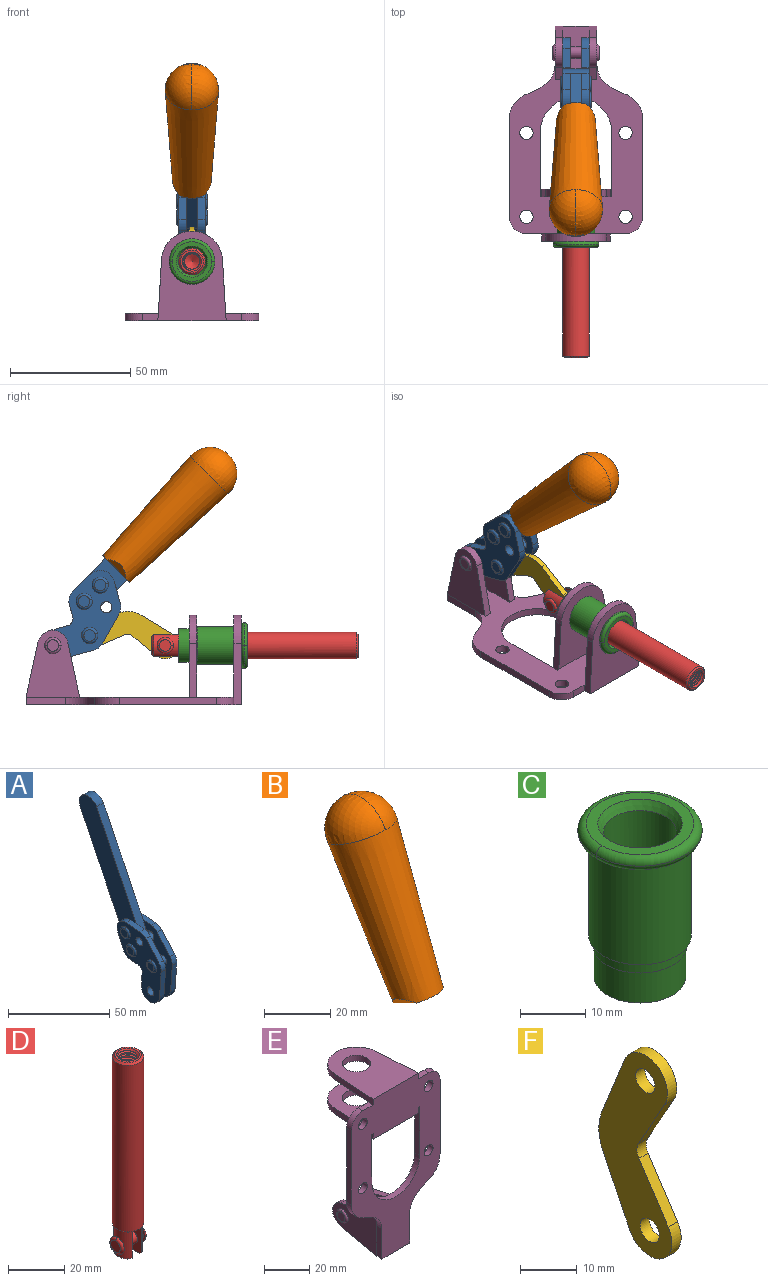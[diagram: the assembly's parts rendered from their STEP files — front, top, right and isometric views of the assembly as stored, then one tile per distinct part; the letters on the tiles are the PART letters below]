
ASSEMBLY  parts=6 mates=6
PART A: 59 faces, bbox 12.9x60.2x99.6 mm
  f0: torus R=2.39mm, axis (-1,0,0), area 14.9mm2, adj f20,f43,f51
  f1: torus R=2.39mm, axis (-1,0,0), area 14.9mm2, adj f19,f42,f51
  f2: torus R=2.39mm, axis (-1,0,0), area 14.9mm2, adj f18,f35,f51
  f3: torus R=2.39mm, axis (-1,0,0), area 14.9mm2, adj f14,f17,f23
  f4: torus R=2.39mm, axis (-1,0,0), area 14.9mm2, adj f13,f16,f23
  f5: torus R=2.39mm, axis (-1,0,0), area 14.9mm2, adj f12,f15,f23
  f6: cylinder r=2.39mm len=4.78mm, axis (1,0,0), area 46.5mm2, adj f48,f50,f51
  f7: cylinder r=2.39mm len=4.78mm, axis (1,0,0), area 46.5mm2, adj f50,f51
  f8: cylinder r=6.35mm len=12.68mm, axis (1,0,0), area 61.8mm2, adj f38,f39,f50,f51
  f9: cylinder r=2.39mm len=4.78mm, axis (-1,0,0), area 70.5mm2, adj f46,f50
  f10: cylinder r=2.39mm len=4.78mm, axis (-1,0,0), area 46.5mm2, adj f23,f45,f46
  f11: cylinder r=2.39mm len=4.78mm, axis (-1,0,0), area 46.5mm2, adj f23,f46
  f12: plane 4.78x4.78mm, normal (1,0,0), area 17.9mm2, adj f5,f15
  f13: plane 4.78x4.78mm, normal (1,0,0), area 17.9mm2, adj f4,f16
  f14: plane 4.78x4.78mm, normal (1,0,0), area 17.9mm2, adj f3,f17
  f15: torus R=2.39mm, axis (-1,0,0), area 14.9mm2, adj f5,f12,f23
  f16: torus R=2.39mm, axis (-1,0,0), area 14.9mm2, adj f4,f13,f23
  f17: torus R=2.39mm, axis (-1,0,0), area 14.9mm2, adj f3,f14,f23
  f18: plane 4.78x4.78mm, normal (-1,0,0), area 17.9mm2, adj f2,f35
  f19: plane 4.78x4.78mm, normal (-1,0,0), area 17.9mm2, adj f1,f42
  f20: plane 4.78x4.78mm, normal (-1,0,0), area 17.9mm2, adj f0,f43
  f21: plane 2.26x0.2mm, normal (1,0,0), area 0.2mm2, adj f31,f44
  f22: plane 2.26x0.2mm, normal (-1,0,0), area 0.2mm2, adj f41,f44
  f23: plane 39.37x30.77mm, normal (1,0,0), area 565.5mm2, adj f3,f4,f5,f10,f11,f15,f16,f17
  f24: cylinder r=6.1mm len=4.15mm, axis (-1,0,0), area 14.7mm2, adj f23,f25,f32,f46
  f25: plane 10.25x9.01mm, normal (0,-0.75,0.66), area 42.3mm2, adj f23,f24,f26,f46
  f26: cylinder r=6.35mm len=4.64mm, axis (-1,0,0), area 15.6mm2, adj f23,f25,f27,f46
  f27: plane 15.84x3.1mm, normal (0,-1,-0.07), area 49.2mm2, adj f23,f26,f28,f46
  f28: cylinder r=6.35mm len=12.68mm, axis (-1,0,0), area 61.8mm2, adj f23,f27,f29,f46
  f29: plane 8.11x3.1mm, normal (0,1,0.07), area 25.2mm2, adj f23,f28,f30,f46
  f30: cylinder r=3.05mm len=3.25mm, axis (-1,0,0), area 14.8mm2, adj f23,f29,f31,f46
  f31: plane 5.99x3.1mm, normal (0,0.07,-1), area 18.6mm2, adj f21,f23,f30,f44,f46
  f32: plane 9.5x3.1mm, normal (0,-0.07,1), area 29.5mm2, adj f23,f24,f33,f46,f47
  f33: cylinder r=6.1mm len=8.63mm, axis (-1,0,0), area 39.1mm2, adj f23,f32,f34,f47
  f34: plane 8.65x3.96mm, normal (0,0.91,-0.42), area 29.5mm2, adj f23,f33,f44,f47
  f35: torus R=2.39mm, axis (-1,0,0), area 14.9mm2, adj f2,f18,f51
  f36: plane 10.25x9.01mm, normal (0,-0.75,0.66), area 42.3mm2, adj f37,f49,f50,f51
  f37: cylinder r=6.35mm len=4.64mm, axis (1,0,0), area 15.6mm2, adj f36,f38,f50,f51
  f38: plane 15.84x3.1mm, normal (0,-1,-0.07), area 49.2mm2, adj f8,f37,f50,f51
  f39: plane 8.11x3.1mm, normal (0,1,0.07), area 25.2mm2, adj f8,f40,f50,f51
  f40: cylinder r=3.05mm len=3.25mm, axis (1,0,0), area 14.8mm2, adj f39,f41,f50,f51
  f41: plane 5.99x3.1mm, normal (0,0.07,-1), area 18.6mm2, adj f22,f40,f44,f50,f51
  f42: torus R=2.39mm, axis (-1,0,0), area 14.9mm2, adj f1,f19,f51
  f43: torus R=2.39mm, axis (-1,0,0), area 14.9mm2, adj f0,f20,f51
  f44: cylinder r=6.35mm len=12.12mm, axis (-1,0,0), area 128.9mm2, adj f21,f22,f23,f31,f34,f41,f46,f47
  f45: plane 2.65x1.35mm, normal (1,0,0), area 1mm2, adj f10,f55
  f46: plane 39.08x20.42mm, normal (-1,0,0), area 412.5mm2, adj f9,f10,f11,f24,f25,f26,f27,f28
  f47: plane 77.62x39.82mm, normal (1,0,0), area 850mm2, adj f32,f33,f34,f44,f53,f54,f55
  f48: plane 2.65x1.35mm, normal (-1,0,0), area 1mm2, adj f6,f55
  f49: cylinder r=6.1mm len=4.15mm, axis (1,0,0), area 14.7mm2, adj f36,f50,f51,f56
  f50: plane 39.08x20.42mm, normal (1,0,0), area 412.5mm2, adj f6,f7,f8,f9,f36,f37,f38,f39
  f51: plane 39.37x30.77mm, normal (-1,0,0), area 565.5mm2, adj f0,f1,f2,f6,f7,f8,f35,f36
  f52: plane 8.65x3.96mm, normal (0,0.91,-0.42), area 29.5mm2, adj f44,f51,f57,f58
  f53: plane 68.49x33.4mm, normal (0,0.9,-0.44), area 358.1mm2, adj f44,f47,f54,f58
  f54: cylinder r=6.35mm len=12.06mm, axis (1,0,0), area 93.7mm2, adj f47,f53,f55,f58
  f55: plane 68.49x33.4mm, normal (0,-0.9,0.44), area 358.1mm2, adj f44,f45,f46,f47,f48,f50,f54,f58
  f56: plane 9.5x3.1mm, normal (0,-0.07,1), area 29.5mm2, adj f49,f50,f51,f57,f58
  f57: cylinder r=6.1mm len=8.63mm, axis (1,0,0), area 39.1mm2, adj f51,f52,f56,f58
  f58: plane 77.62x39.82mm, normal (-1,0,0), area 850mm2, adj f44,f52,f53,f54,f55,f56,f57
PART B: 11 faces, bbox 22.3x42.6x64.5 mm
  f0: sphere r=11.13mm, area 411.4mm2, adj f1,f8
  f1: cone r=11.11mm half-angle=3.3deg, axis (0,0.44,0.9), area 3251.8mm2, adj f0,f7,f8,f9,f10
  f2: cylinder r=6.16mm len=11.7mm, axis (1,0,0), area 89.5mm2, adj f3,f4,f5,f6
  f3: plane 60.23x36.75mm, normal (-1,0,0), area 763.6mm2, adj f2,f4,f6,f10
  f4: plane 51.37x25.05mm, normal (0,0.9,-0.44), area 264.2mm2, adj f2,f3,f5,f10
  f5: plane 60.23x36.75mm, normal (1,0,0), area 763.6mm2, adj f2,f4,f6,f10
  f6: plane 51.37x25.05mm, normal (0,-0.9,0.44), area 264.2mm2, adj f2,f3,f5,f10
  f7: plane 9.95x5.95mm, normal (0.71,-0.31,-0.64), area 25.8mm2, adj f1,f10
  f8: sphere r=11.13mm, area 411.4mm2, adj f0,f1
  f9: plane 9.95x5.95mm, normal (-0.71,-0.31,-0.64), area 25.8mm2, adj f1,f10
  f10: plane 14.27x11.38mm, normal (0,-0.44,-0.9), area 106.7mm2, adj f1,f3,f4,f5,f6,f7,f9
PART C: 15 faces, bbox 20.6x20.6x28.7 mm
  f0: torus R=8.26mm, axis (0,0,1), area 56.8mm2, adj f1,f10,f12
  f1: torus R=8.26mm, axis (0,0,1), area 56.8mm2, adj f0,f6,f13
  f2: cylinder r=5.59mm len=25.91mm, axis (0,0,1), area 909.6mm2, adj f3,f4
  f3: cone r=6.86mm half-angle=45deg, axis (0,0,-1), area 70.2mm2, adj f2,f14
  f4: cone r=6.47mm half-angle=30deg, axis (0,0,1), area 66.7mm2, adj f2,f13
  f5: cylinder r=7.04mm len=14.07mm, axis (0,0,1), area 252.6mm2, adj f11,f14
  f6: torus R=8.26mm, axis (0,0,1), area 56.8mm2, adj f1,f12,f13
  f7: cylinder r=7.16mm len=14.33mm, axis (0,0,1), area 91.5mm2, adj f9,f11
  f8: cylinder r=7.86mm len=18.42mm, axis (0,0,1), area 909.6mm2, adj f9,f10
  f9: plane 15.72x15.72mm, normal (0,0,-1), area 33mm2, adj f7,f8
  f10: plane 16.51x16.51mm, normal (0,0,-1), area 19.9mm2, adj f0,f8,f12
  f11: plane 14.33x14.33mm, normal (0,0,-1), area 5.7mm2, adj f5,f7
  f12: torus R=8.26mm, axis (0,0,1), area 56.8mm2, adj f0,f6,f10
  f13: plane 16.51x16.51mm, normal (0,0,1), area 82.7mm2, adj f1,f4,f6
  f14: plane 14.07x14.07mm, normal (0,0,-1), area 7.8mm2, adj f3,f5
PART D: 48 faces, bbox 12.6x11.1x86.1 mm
  f0: torus R=2.41mm, axis (-1,0,0), area 15mm2, adj f30,f32,f34
  f1: torus R=2.41mm, axis (-1,0,0), area 15mm2, adj f29,f31,f33
  f2: cylinder r=5.54mm len=72.39mm, axis (0,0,1), area 2518.5mm2, adj f3,f4,f42,f43
  f3: cone r=5.54mm half-angle=45deg, axis (0,0,1), area 7.6mm2, adj f2,f5,f41
  f4: cone r=5.54mm half-angle=45deg, axis (0,0,-1), area 34.9mm2, adj f2,f39
  f5: cylinder r=5.08mm len=11.48mm, axis (0,0,1), area 108.3mm2, adj f3,f7,f8,f41
  f6: cylinder r=2.41mm len=4.83mm, axis (-1,0,0), area 71.2mm2, adj f40,f41
  f7: cylinder r=2.41mm len=4.83mm, axis (-1,0,0), area 7.6mm2, adj f5,f34
  f8: cone r=5.08mm half-angle=45deg, axis (0,0,1), area 10.6mm2, adj f5,f37,f41
  f9: cone r=3.98mm half-angle=45deg, axis (0,0,1), area 17.6mm2, adj f27,f39,f45,f46,f47
  f10: cylinder r=2.41mm len=4.83mm, axis (-1,0,0), area 7.6mm2, adj f33,f38
  f11: cylinder r=3.2mm len=6.4mm, axis (0,0,1), area 78.4mm2, adj f12,f28,f44,f45,f47
  f12: cylinder r=3.2mm len=6.4mm, axis (0,0,1), area 10.5mm2, adj f11,f13,f45,f47
  f13: cylinder r=3.2mm len=6.4mm, axis (0,0,1), area 10.5mm2, adj f12,f14,f45,f47
  f14: cylinder r=3.2mm len=6.4mm, axis (0,0,1), area 10.5mm2, adj f13,f15,f45,f47
  f15: cylinder r=3.2mm len=6.4mm, axis (0,0,1), area 10.5mm2, adj f14,f16,f45,f47
  f16: cylinder r=3.2mm len=6.4mm, axis (0,0,1), area 10.5mm2, adj f15,f17,f45,f47
  f17: cylinder r=3.2mm len=6.4mm, axis (0,0,1), area 10.5mm2, adj f16,f18,f45,f47
  f18: cylinder r=3.2mm len=6.4mm, axis (0,0,1), area 10.5mm2, adj f17,f19,f45,f47
  f19: cylinder r=3.2mm len=6.4mm, axis (0,0,1), area 10.5mm2, adj f18,f20,f45,f47
  f20: cylinder r=3.2mm len=6.4mm, axis (0,0,1), area 10.5mm2, adj f19,f21,f45,f47
  f21: cylinder r=3.2mm len=6.4mm, axis (0,0,1), area 10.5mm2, adj f20,f22,f45,f47
  f22: cylinder r=3.2mm len=6.4mm, axis (0,0,1), area 10.5mm2, adj f21,f23,f45,f47
  f23: cylinder r=3.2mm len=6.4mm, axis (0,0,1), area 10.5mm2, adj f22,f24,f45,f47
  f24: cylinder r=3.2mm len=6.4mm, axis (0,0,1), area 10.5mm2, adj f23,f25,f45,f47
  f25: cylinder r=3.2mm len=6.4mm, axis (0,0,1), area 10.5mm2, adj f24,f26,f45,f47
  f26: cylinder r=3.2mm len=6.4mm, axis (0,0,1), area 10.5mm2, adj f25,f27,f45,f47
  f27: cylinder r=3.2mm len=6.4mm, axis (0,0,1), area 7.4mm2, adj f9,f26,f45,f47
  f28: cone r=3.2mm half-angle=60deg, axis (0,0,1), area 37.2mm2, adj f11
  f29: plane 4.83x4.83mm, normal (-1,0,0), area 18.3mm2, adj f1,f31
  f30: plane 4.83x4.83mm, normal (1,0,0), area 18.3mm2, adj f0,f32
  f31: torus R=2.41mm, axis (-1,0,0), area 15mm2, adj f1,f29,f33
  f32: torus R=2.41mm, axis (-1,0,0), area 15mm2, adj f0,f30,f34
  f33: plane 6.83x6.83mm, normal (1,0,0), area 18.3mm2, adj f1,f10,f31
  f34: plane 6.83x6.83mm, normal (-1,0,0), area 18.3mm2, adj f0,f7,f32
  f35: cone r=5.08mm half-angle=45deg, axis (0,0,1), area 10.6mm2, adj f36,f38,f40
  f36: plane 7.25x1.97mm, normal (0,0,-1), area 10mm2, adj f35,f40
  f37: plane 7.25x1.97mm, normal (0,0,-1), area 10mm2, adj f8,f41
  f38: cylinder r=5.08mm len=11.48mm, axis (0,0,1), area 108.3mm2, adj f10,f35,f40,f42
  f39: plane 9.55x9.55mm, normal (0,0,1), area 22mm2, adj f4,f9
  f40: plane 12.76x10.09mm, normal (1,0,0), area 95.7mm2, adj f6,f35,f36,f38,f42,f43
  f41: plane 12.76x10.09mm, normal (-1,0,0), area 95.7mm2, adj f3,f5,f6,f8,f37,f43
  f42: cone r=5.54mm half-angle=45deg, axis (0,0,1), area 7.6mm2, adj f2,f38,f40
  f43: plane 11.07x4.7mm, normal (0,0,-1), area 50.4mm2, adj f2,f40,f41
  f44: plane 0.89x0.62mm, normal (-1,0,0), area 0.3mm2, adj f11,f45,f46,f47
  f45: bspline ~24.8x7.63mm, area 266.6mm2, adj f9,f11,f12,f13,f14,f15,f16,f17
  f46: bspline ~24.87x7.63mm, area 73.6mm2, adj f9,f44,f45,f47
  f47: bspline ~24.98x7.63mm, area 272.5mm2, adj f9,f11,f12,f13,f14,f15,f16,f17
PART E: 55 faces, bbox 55.7x37.4x89.8 mm
  f0: torus R=2.41mm, axis (-1,0,0), area 15mm2, adj f11,f15,f25
  f1: torus R=2.41mm, axis (-1,0,0), area 15mm2, adj f10,f12,f22
  f2: cylinder r=2.78mm len=5.56mm, axis (0,-1,0), area 54.2mm2, adj f30,f54
  f3: cylinder r=14.99mm len=29.97mm, axis (0,-1,0), area 145.9mm2, adj f30,f49,f53,f54
  f4: cylinder r=2.78mm len=5.56mm, axis (0,-1,0), area 54.2mm2, adj f30,f54
  f5: cylinder r=2.78mm len=5.56mm, axis (0,-1,0), area 54.2mm2, adj f30,f54
  f6: cylinder r=2.78mm len=5.56mm, axis (0,-1,0), area 54.2mm2, adj f30,f54
  f7: cylinder r=6.35mm len=12.7mm, axis (0,0,1), area 123.6mm2, adj f27,f51
  f8: cylinder r=6.35mm len=12.7mm, axis (0,0,-1), area 124.7mm2, adj f21,f35
  f9: cylinder r=2.41mm len=11.18mm, axis (-1,0,0), area 169.4mm2, adj f16,f19
  f10: plane 4.83x4.83mm, normal (1,0,0), area 18.3mm2, adj f1,f12
  f11: plane 4.83x4.83mm, normal (-1,0,0), area 18.3mm2, adj f0,f15
  f12: torus R=2.41mm, axis (-1,0,0), area 15mm2, adj f1,f10,f22
  f13: cylinder r=6.35mm len=12.41mm, axis (1,0,0), area 53.4mm2, adj f18,f19,f22,f23
  f14: cylinder r=6.35mm len=12.41mm, axis (-1,0,0), area 53.4mm2, adj f16,f17,f24,f25
  f15: torus R=2.41mm, axis (-1,0,0), area 15mm2, adj f0,f11,f25
  f16: plane 27.86x22.35mm, normal (1,0,0), area 425.4mm2, adj f9,f14,f17,f24,f30
  f17: plane 22.86x4.97mm, normal (0,0.21,0.98), area 72.5mm2, adj f14,f16,f25,f30
  f18: plane 22.86x4.97mm, normal (0,0.21,0.98), area 72.5mm2, adj f13,f19,f22,f30
  f19: plane 27.86x22.35mm, normal (-1,0,0), area 425.4mm2, adj f9,f13,f18,f23,f30
  f20: cylinder r=12.7mm len=25.35mm, axis (0,0,-1), area 119.8mm2, adj f21,f34,f35,f36
  f21: plane 34.21x28.07mm, normal (0,0,-1), area 702.4mm2, adj f8,f20,f30,f34,f36
  f22: plane 27.96x22.45mm, normal (1,0,0), area 407.2mm2, adj f1,f12,f13,f18,f23,f30,f42,f43
  f23: plane 22.86x4.97mm, normal (0,0.21,-0.98), area 72.5mm2, adj f13,f19,f22,f44
  f24: plane 22.86x4.97mm, normal (0,0.21,-0.98), area 72.5mm2, adj f14,f16,f25,f44
  f25: plane 27.86x22.35mm, normal (-1,0,0), area 407.1mm2, adj f0,f14,f15,f17,f24,f30,f45,f46
  f26: plane 3.1x0.95mm, normal (0,0,-1), area 2.7mm2, adj f30,f49,f50,f54
  f27: plane 34.21x28.07mm, normal (0,0,1), area 702.4mm2, adj f7,f28,f30,f50,f52
  f28: cylinder r=12.7mm len=25.35mm, axis (0,0,1), area 118.8mm2, adj f27,f50,f51,f52
  f29: plane 3.1x0.95mm, normal (0,0,-1), area 2.7mm2, adj f30,f52,f53,f54
  f30: plane 86.54x55.63mm, normal (0,1,0), area 2362.9mm2, adj f2,f3,f4,f5,f6,f16,f17,f18
  f31: plane 40.56x3.1mm, normal (-1,0,0), area 125.7mm2, adj f30,f32,f48,f54
  f32: cylinder r=7.11mm len=7.11mm, axis (0,-1,0), area 34.6mm2, adj f30,f31,f33,f54
  f33: plane 6.67x3.1mm, normal (0,0,1), area 20.4mm2, adj f30,f32,f34,f54
  f34: plane 25.39x3.13mm, normal (-1,0.06,0), area 79.5mm2, adj f20,f21,f33,f35,f54
  f35: plane 37.31x28.45mm, normal (0,0,1), area 789.9mm2, adj f8,f20,f34,f36,f54
  f36: plane 25.39x3.13mm, normal (1,0.06,0), area 79.5mm2, adj f20,f21,f35,f37,f54
  f37: plane 6.67x3.1mm, normal (0,0,1), area 20.4mm2, adj f30,f36,f38,f54
  f38: cylinder r=7.11mm len=7.11mm, axis (0,-1,0), area 34.6mm2, adj f30,f37,f39,f54
  f39: plane 40.56x3.1mm, normal (1,0,0), area 125.7mm2, adj f30,f38,f40,f54
  f40: cylinder r=11.18mm len=10.16mm, axis (0,-1,0), area 39.5mm2, adj f30,f39,f41,f54
  f41: plane 6.09x3.1mm, normal (0.42,0,-0.91), area 20.8mm2, adj f30,f40,f42,f54
  f42: cylinder r=11.18mm len=9.41mm, axis (0,-1,0), area 37.2mm2, adj f22,f30,f41,f43,f54
  f43: plane 16.5x3.1mm, normal (1,0,0), area 51.1mm2, adj f22,f42,f44,f54
  f44: plane 17.37x3.1mm, normal (0,0,-1), area 53.8mm2, adj f23,f24,f30,f43,f45,f54
  f45: plane 16.5x3.1mm, normal (-1,0,0), area 51.1mm2, adj f25,f44,f46,f54
  f46: cylinder r=11.18mm len=9.41mm, axis (0,-1,0), area 37.2mm2, adj f25,f30,f45,f47,f54
  f47: plane 6.09x3.1mm, normal (-0.42,0,-0.91), area 20.8mm2, adj f30,f46,f48,f54
  f48: cylinder r=11.18mm len=10.16mm, axis (0,-1,0), area 39.5mm2, adj f30,f31,f47,f54
  f49: plane 26.54x3.1mm, normal (-1,0,0), area 82.3mm2, adj f3,f26,f30,f54
  f50: plane 25.39x3.1mm, normal (1,0.06,0), area 78.8mm2, adj f26,f27,f28,f51,f54
  f51: plane 37.31x28.45mm, normal (0,0,-1), area 789.9mm2, adj f7,f28,f50,f52,f54
  f52: plane 25.39x3.1mm, normal (-1,0.06,0), area 78.8mm2, adj f27,f28,f29,f51,f54
  f53: plane 26.54x3.1mm, normal (1,0,0), area 82.3mm2, adj f3,f29,f30,f54
  f54: plane 89.66x55.63mm, normal (0,-1,0), area 2678.5mm2, adj f2,f3,f4,f5,f6,f26,f29,f31
PART F: 12 faces, bbox 2.3x18.2x42.8 mm
  f0: cylinder r=2.4mm len=4.8mm, axis (1,0,0), area 34.9mm2, adj f4,f11
  f1: cylinder r=10.41mm len=8.47mm, axis (1,0,0), area 20.2mm2, adj f4,f9,f10,f11
  f2: cylinder r=3.05mm len=3.16mm, axis (1,0,0), area 7.7mm2, adj f4,f6,f7,f11
  f3: cylinder r=2.4mm len=4.8mm, axis (1,0,0), area 34.9mm2, adj f4,f11
  f4: plane 42.81x18.23mm, normal (-1,0,0), area 414.1mm2, adj f0,f1,f2,f3,f5,f6,f7,f8
  f5: cylinder r=5.54mm len=10.67mm, axis (1,0,0), area 41.8mm2, adj f4,f6,f10,f11
  f6: plane 11.66x6.53mm, normal (0,-0.87,-0.49), area 30.9mm2, adj f2,f4,f5,f11
  f7: plane 11.17x7.33mm, normal (0,-0.84,0.55), area 30.9mm2, adj f2,f4,f8,f11
  f8: cylinder r=5.54mm len=10.51mm, axis (1,0,0), area 41.8mm2, adj f4,f7,f9,f11
  f9: plane 13.67x6.67mm, normal (0,0.9,-0.44), area 35.1mm2, adj f1,f4,f8,f11
  f10: plane 14.1x5.7mm, normal (0,0.93,0.37), area 35.1mm2, adj f1,f4,f5,f11
  f11: plane 42.81x18.23mm, normal (1,0,0), area 414.1mm2, adj f0,f1,f2,f3,f5,f6,f7,f8
PLACE A rot(axis=(1,0,0),70.7deg) t=(0,-5.11,8.91)mm
PLACE B rot(axis=(1,0,0),70.7deg) t=(-0.04,-5.11,8.91)mm
PLACE C rot(axis=(1,0,0),90deg) t=(0,1.23,-3.1)mm
PLACE D rot(axis=(1,0,0),90deg) t=(0,2.02,-3.1)mm
PLACE E rot(axis=(1,0,0),90deg) t=(0,1.23,-3.1)mm fixed
PLACE F rot(axis=(1,0,0),99.6deg) t=(0,5.9,-0.18)mm
MATE slider D.f2 <-> C.f2  axis (0,-1,0) through (0,-56.76,21.51)mm
MATE fastened B.f2 <-> A.f54  axis (1,0,0) through (-2.35,-33.28,94.07)mm
MATE revolute A.f7 <-> E.f0  axis (-1,0,0) through (0,33.32,21.51)mm
MATE fastened C.f0 <-> E.f7  axis (0,1,0) through (0,-45.16,21.51)mm
MATE revolute A.f4 <-> F.f3  axis (-1,0,0) through (0,18.01,25.71)mm
MATE revolute F.f5 <-> D.f6  axis (1,0,0) through (0,-13.46,21.51)mm
